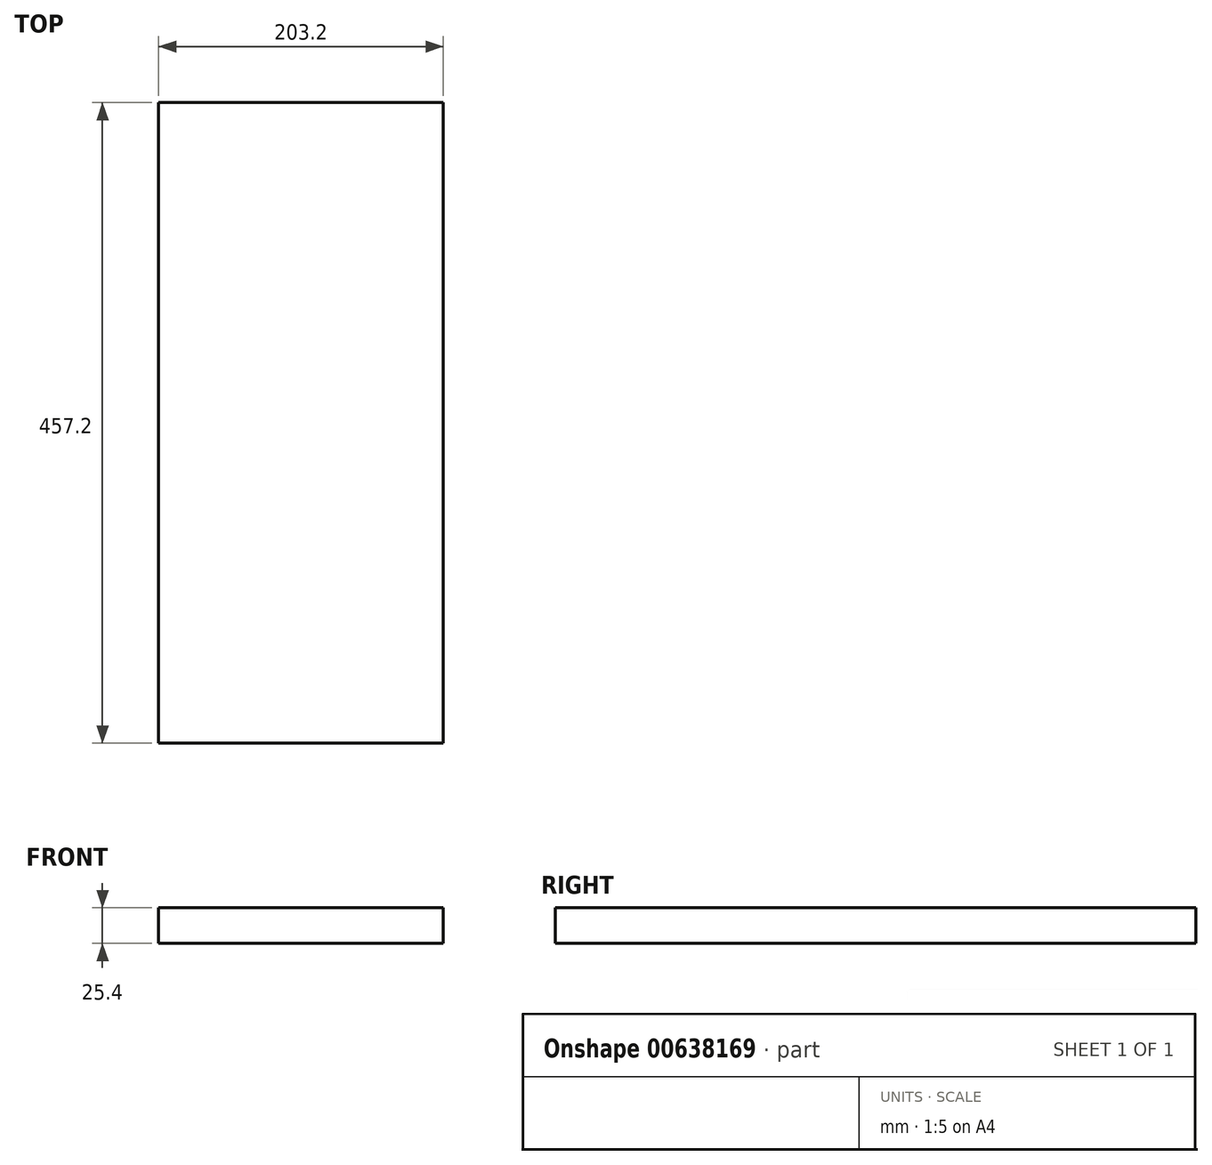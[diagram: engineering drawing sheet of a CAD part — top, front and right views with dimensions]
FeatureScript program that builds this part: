
annotation { "Feature Type Name" : "Feature", "Feature Type Description" : "" }
export const myFeature = defineFeature(function(context is Context, id is Id, definition is map)
    precondition{}
    {
        {
            var Q0;
            Q0=qCreatedBy(makeId("Top.planeOp"),FACE);
            var sketch = newSketch(context, id + "F0", { "sketchPlane" : qUnion([Q0])});
            skLineSegment(sketch, "E0.bottom", {"start": v(-69.4, 449.7) * mm, "end": v(133.8, 449.7) * mm});
            skLineSegment(sketch, "E0.top", {"start": v(-69.4, -7.5) * mm, "end": v(133.8, -7.5) * mm});
            skLineSegment(sketch, "E0.left", {"start": v(-69.4, 449.7) * mm, "end": v(-69.4, -7.5) * mm});
            skLineSegment(sketch, "E0.right", {"start": v(133.8, 449.7) * mm, "end": v(133.8, -7.5) * mm});
            skSolve(sketch);
        }
        {
            var Q0;
            Q0=makeQuery(id+"F0.imprint","IMPRINT",FACE,{"disambiguationData":[TD([[makeQuery(id+"F0.imprint","IMPRINT",EDGE,{"derivedFrom":sQuery(id+"F0.wireOp",EDGE,"E0.bottom")}),-1.0]])]});
            extrude(context, id + "F1", {"entities" : qUnion([Q0]), "depth" : 25.4 * mm, "offsetDistance" : 25.4 * mm});
        }
    });
